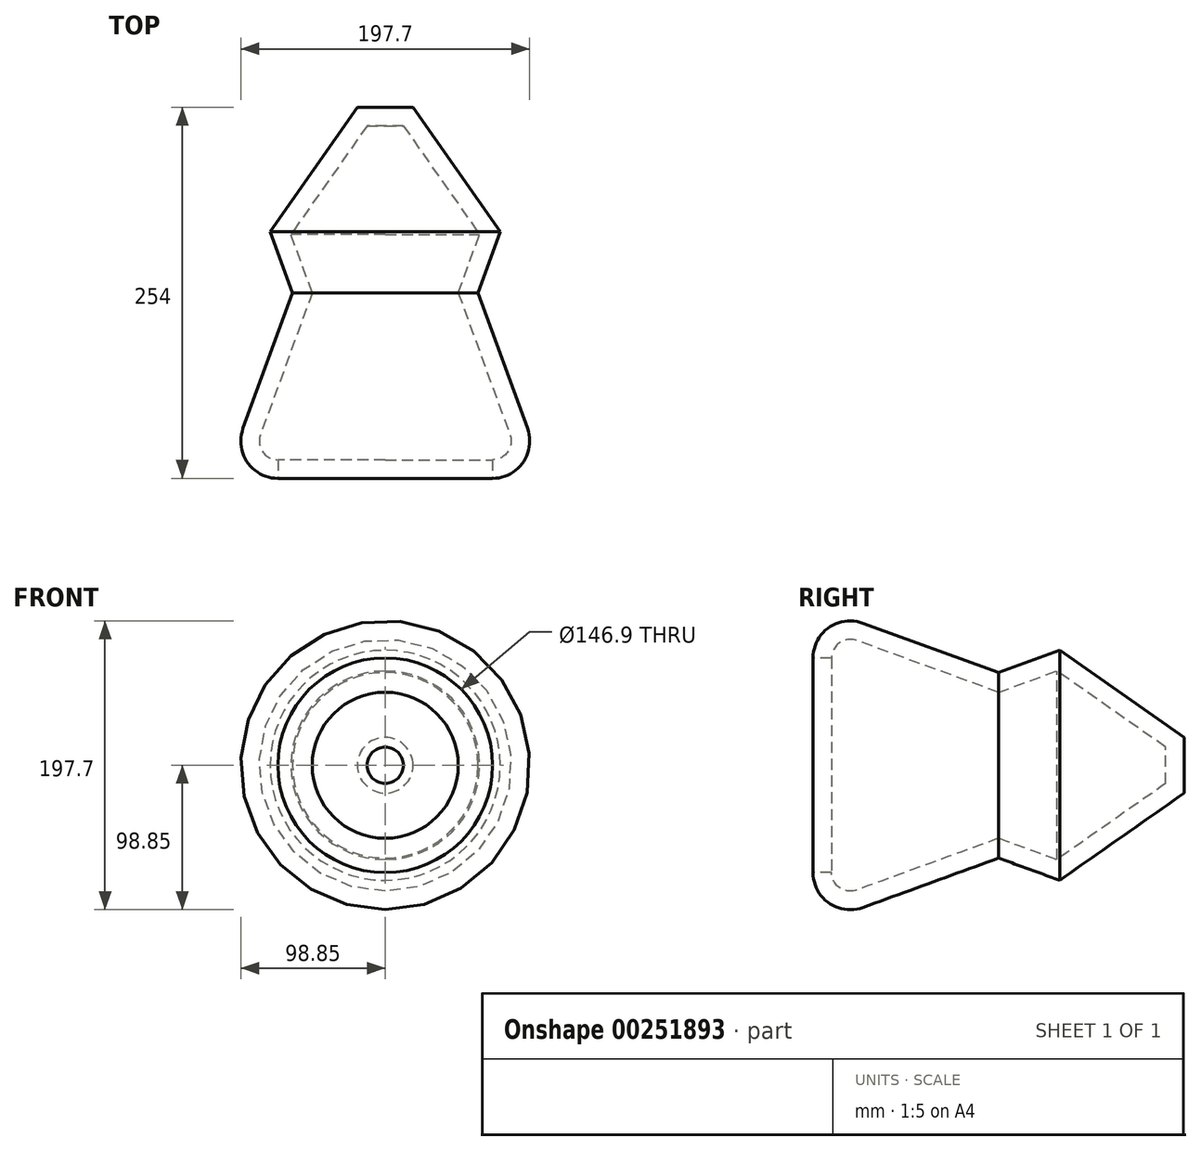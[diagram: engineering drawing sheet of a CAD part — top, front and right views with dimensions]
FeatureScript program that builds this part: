
annotation { "Feature Type Name" : "Feature", "Feature Type Description" : "" }
export const myFeature = defineFeature(function(context is Context, id is Id, definition is map)
    precondition{}
    {
        {
            var Q0;
            Q0=qCreatedBy(makeId("Front.planeOp"),FACE);
            var sketch = newSketch(context, id + "F0", { "sketchPlane" : qUnion([Q0])});
            skCircle(sketch, "E0", {"center": v(0, 0) * mm, "radius": 63.5 * mm});
            skSolve(sketch);
        }
        {
            var Q0;
            Q0=makeQuery(id+"F0.imprint","IMPRINT",FACE,{"disambiguationData":[TD([[makeQuery(id+"F0.imprint","IMPRINT",EDGE,{"derivedFrom":sQuery(id+"F0.wireOp",EDGE,"E0")}),1.0]])]});
            extrude(context, id + "F1", {"entities" : qUnion([Q0]), "endBound" : BoundingType.SYMMETRIC, "depth" : 254 * mm, "hasDraft" : true, "draftAngle" : 20 * degree});
        }
        {
            var Q0;
            Q0=makeQuery(id+"F1.opExtrude","CAP_FACE",FACE,{"disambiguationData":[OSD([sQuery(id+"F0.wireOp",EDGE,"E0")])],"isStart":false});
            fillet(context, id + "F2", {"entities" : qUnion([Q0]), "radius" : 25.4 * mm, "tangentPropagation" : true, "allowEdgeOverflow" : false});
        }
        {
            var Q0;
            Q0=makeQuery(id+"F1.opExtrude","CAP_EDGE",EDGE,{"disambiguationData":[OSD([sQuery(id+"F0.wireOp",EDGE,"E0")])],"isStart":true});
            var Q1;
            Q1=makeQuery(id+"F1.opExtrude","CAP_FACE",FACE,{"disambiguationData":[OSD([sQuery(id+"F0.wireOp",EDGE,"E0")])],"isStart":true});
            chamfer(context, id + "F3", {"entities" : qUnion([Q0, Q1]), "width" : 63.5 * mm, "tangentPropagation" : true});
        }
        {
            var Q0;
            Q0=makeQuery(id+"F1.opExtrude","CAP_FACE",FACE,{"disambiguationData":[OSD([sQuery(id+"F0.wireOp",EDGE,"E0")])],"isStart":false});
            shell(context, id + "F4", {"entities" : qUnion([Q0]), "thickness" : 12.7 * mm});
        }
    });
